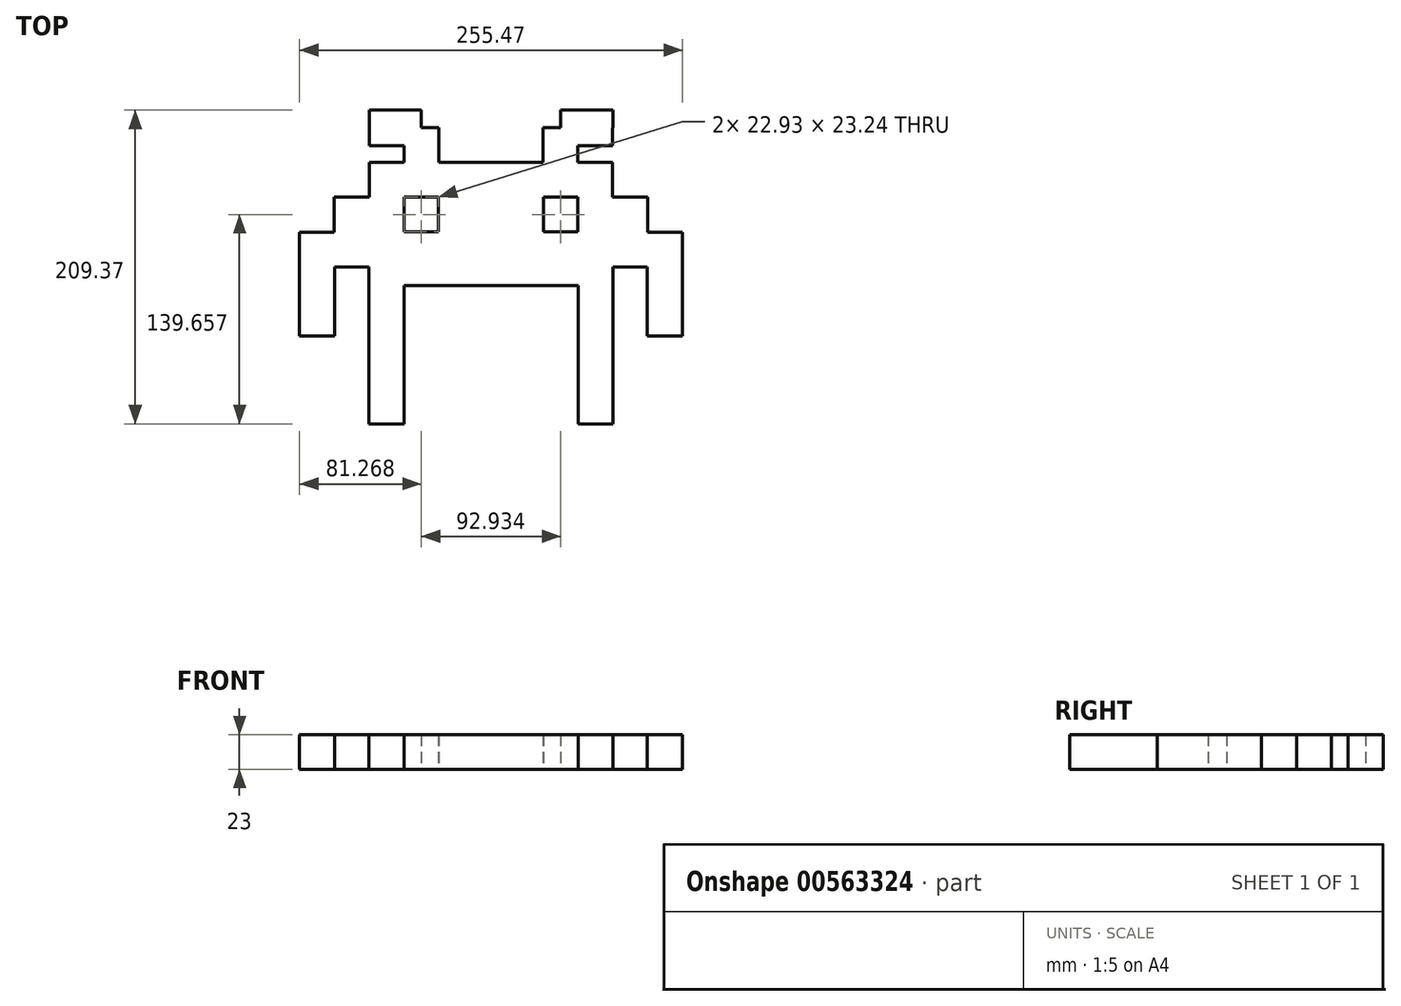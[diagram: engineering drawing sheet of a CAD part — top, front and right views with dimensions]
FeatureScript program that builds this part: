
annotation { "Feature Type Name" : "Feature", "Feature Type Description" : "" }
export const myFeature = defineFeature(function(context is Context, id is Id, definition is map)
    precondition{}
    {
        {
            var Q0;
            Q0=qCreatedBy(makeId("Top.planeOp"),FACE);
            var sketch = newSketch(context, id + "F0", { "sketchPlane" : qUnion([Q0])});
            skLineSegment(sketch, "E0", {"start": v(81.47, 72) * mm, "end": v(46.62, 72) * mm});
            skLineSegment(sketch, "E1", {"start": v(46.62, 72) * mm, "end": v(46.62, 60.31) * mm});
            skLineSegment(sketch, "E2", {"start": v(46.62, 60.31) * mm, "end": v(34.89, 60.31) * mm});
            skLineSegment(sketch, "E3", {"start": v(34.89, 60.31) * mm, "end": v(34.89, 37.15) * mm});
            skLineSegment(sketch, "E4", {"start": v(34.89, 37.15) * mm, "end": v(0.18, 37.15) * mm});
            skLineSegment(sketch, "E5", {"start": v(0.18, 37.15) * mm, "end": v(0.18, -45.09) * mm});
            skLineSegment(sketch, "E6", {"start": v(0.18, -45.09) * mm, "end": v(58.27, -45.09) * mm});
            skLineSegment(sketch, "E7", {"start": v(58.27, -45.09) * mm, "end": v(58.27, -137.37) * mm});
            skLineSegment(sketch, "E8", {"start": v(58.27, -137.37) * mm, "end": v(81.65, -137.37) * mm});
            skLineSegment(sketch, "E9", {"start": v(81.65, -137.37) * mm, "end": v(81.65, -32.66) * mm});
            skLineSegment(sketch, "E10", {"start": v(81.65, -32.66) * mm, "end": v(104.54, -32.66) * mm});
            skLineSegment(sketch, "E11", {"start": v(104.54, -32.66) * mm, "end": v(104.54, -78.88) * mm});
            skLineSegment(sketch, "E12", {"start": v(104.54, -78.88) * mm, "end": v(127.92, -78.88) * mm});
            skLineSegment(sketch, "E13", {"start": v(127.92, -78.88) * mm, "end": v(127.92, -9.38) * mm});
            skLineSegment(sketch, "E14", {"start": v(127.92, -9.38) * mm, "end": v(104.68, -9.38) * mm});
            skLineSegment(sketch, "E15", {"start": v(104.68, -9.38) * mm, "end": v(104.68, 14) * mm});
            skLineSegment(sketch, "E16", {"start": v(104.68, 14) * mm, "end": v(81.3, 14) * mm});
            skLineSegment(sketch, "E17", {"start": v(81.3, 14) * mm, "end": v(81.3, 37.15) * mm});
            skLineSegment(sketch, "E18", {"start": v(81.3, 37.15) * mm, "end": v(58.07, 37.15) * mm});
            skLineSegment(sketch, "E19", {"start": v(58.07, 37.15) * mm, "end": v(58.07, 48.37) * mm});
            skLineSegment(sketch, "E20", {"start": v(58.07, 48.37) * mm, "end": v(81.3, 48.37) * mm});
            skLineSegment(sketch, "E21", {"start": v(81.3, 48.37) * mm, "end": v(81.47, 72) * mm});
            skLineSegment(sketch, "E22", {"start": v(58.12, -9.33) * mm, "end": v(35.19, -9.33) * mm});
            skLineSegment(sketch, "E23", {"start": v(35.19, -9.33) * mm, "end": v(35.19, 13.9) * mm});
            skLineSegment(sketch, "E24", {"start": v(35.19, 13.9) * mm, "end": v(58.12, 13.9) * mm});
            skLineSegment(sketch, "E25", {"start": v(58.12, 13.9) * mm, "end": v(58.12, -9.33) * mm});
            skLineSegment(sketch, "E26.MirrorCS", {"start": v(-46.25, 72) * mm, "end": v(-46.25, 60.31) * mm});
            skLineSegment(sketch, "E27.MirrorCS", {"start": v(-57.7, 37.15) * mm, "end": v(-57.7, 48.37) * mm});
            skLineSegment(sketch, "E28.MirrorCS", {"start": v(-46.25, 60.31) * mm, "end": v(-34.52, 60.31) * mm});
            skLineSegment(sketch, "E29.MirrorCS", {"start": v(-34.82, 13.9) * mm, "end": v(-57.75, 13.9) * mm});
            skLineSegment(sketch, "E30.MirrorCS", {"start": v(-57.9, -45.09) * mm, "end": v(-57.9, -137.37) * mm});
            skLineSegment(sketch, "E31.MirrorCS", {"start": v(-57.75, -9.33) * mm, "end": v(-34.82, -9.33) * mm});
            skLineSegment(sketch, "E32.MirrorCS", {"start": v(-57.75, 13.9) * mm, "end": v(-57.75, -9.33) * mm});
            skLineSegment(sketch, "E33.MirrorCS", {"start": v(-80.93, 48.37) * mm, "end": v(-81.1, 72) * mm});
            skLineSegment(sketch, "E34.MirrorCS", {"start": v(-80.93, 14) * mm, "end": v(-80.93, 37.15) * mm});
            skLineSegment(sketch, "E35.MirrorCS", {"start": v(-127.55, -78.88) * mm, "end": v(-127.55, -9.38) * mm});
            skLineSegment(sketch, "E36.MirrorCS", {"start": v(-127.55, -9.38) * mm, "end": v(-104.31, -9.38) * mm});
            skLineSegment(sketch, "E37.MirrorCS", {"start": v(-104.31, -9.38) * mm, "end": v(-104.31, 14) * mm});
            skLineSegment(sketch, "E38.MirrorCS", {"start": v(-80.93, 37.15) * mm, "end": v(-57.7, 37.15) * mm});
            skLineSegment(sketch, "E39.MirrorCS", {"start": v(-81.1, 72) * mm, "end": v(-46.25, 72) * mm});
            skLineSegment(sketch, "E40.MirrorCS", {"start": v(-34.52, 60.31) * mm, "end": v(-34.52, 37.15) * mm});
            skLineSegment(sketch, "E41.MirrorCS", {"start": v(-34.52, 37.15) * mm, "end": v(0.18, 37.15) * mm});
            skLineSegment(sketch, "E42.MirrorCS", {"start": v(-81.28, -137.37) * mm, "end": v(-81.28, -32.66) * mm});
            skLineSegment(sketch, "E43.MirrorCS", {"start": v(-81.28, -32.66) * mm, "end": v(-104.17, -32.66) * mm});
            skLineSegment(sketch, "E44.MirrorCS", {"start": v(-57.9, -137.37) * mm, "end": v(-81.28, -137.37) * mm});
            skLineSegment(sketch, "E45.MirrorCS", {"start": v(-104.31, 14) * mm, "end": v(-80.93, 14) * mm});
            skLineSegment(sketch, "E46.MirrorCS", {"start": v(-57.7, 48.37) * mm, "end": v(-80.93, 48.37) * mm});
            skLineSegment(sketch, "E47.MirrorCS", {"start": v(-34.82, -9.33) * mm, "end": v(-34.82, 13.9) * mm});
            skLineSegment(sketch, "E48.MirrorCS", {"start": v(-104.17, -78.88) * mm, "end": v(-127.55, -78.88) * mm});
            skLineSegment(sketch, "E49.MirrorCS", {"start": v(-104.17, -32.66) * mm, "end": v(-104.17, -78.88) * mm});
            skLineSegment(sketch, "E50.MirrorCS", {"start": v(0.18, -45.09) * mm, "end": v(-57.9, -45.09) * mm});
            skSolve(sketch);
        }
        {
            var Q0;
            Q0=makeQuery(id+"F0.imprint","IMPRINT",FACE,{"disambiguationData":[TD([[makeQuery(id+"F0.imprint","IMPRINT",EDGE,{"derivedFrom":sQuery(id+"F0.wireOp",EDGE,"E0")}),1.0]])]});
            var Q1;
            Q1=makeQuery(id+"F0.imprint","IMPRINT",FACE,{"disambiguationData":[TD([[makeQuery(id+"F0.imprint","IMPRINT",EDGE,{"derivedFrom":sQuery(id+"F0.wireOp",EDGE,"E5")}),-1.0]])]});
            extrude(context, id + "F1", {"entities" : qUnion([Q0, Q1]), "depth" : 23 * mm, "offsetDistance" : 25 * mm});
        }
    });
